# Revit family: NBS_Allermuir_OffcChrs-en-us-Kin_HighBackStool
name_source: partatom
category: Furniture
revit_build: Autodesk Revit 2018 (Build: 20190510_1515(x64)
units: mm (PartAtom-declared; Revit-internal decimal feet)

## family parameters
Always vertical = Yes
Cut with Voids When Loaded = No
Room Calculation Point = No
Shared = No
Work Plane-Based = No

## types (1)
- Kin_HighBackStool_KIN602
    AssetType = Movable
    BIMObjectName = NBS_Allermuir_OfficeChairs_Kin_HighBackStool_KIN602-US
    Category = Pr_40_50_12_57:Office chairs
    CodePerformance = ANSI/BIFMA X5.1-2017
    Color = Off-Black, White, Crayon Gray, Pistachio, Haze Blue, Aubergine, Seattle Green, Red
    Description = High back stool on 4 leg frame
    DurationUnit = year
    ExpectedLife = 10
    Features = Plastic shell — color: Off-Black, Tubular steel frame finished in Off-Black powder coat, Footrest protector, Plastic glides, Counter height option available, Plastic glides with felt
    Finish = Off-Black, White, Crayon Gray, Pistachio, Haze Blue, Aubergine, Seattle Green, Red
    FrameFinish = Off black, white, crayon gray, pistachio, seattle green, aubergine, red, haze blue
    FrameMaterial = NBS_Allermuir_Steel_BlackPowderCoat
    HighestSeatingHeight = 0 "
    IfcExportAs = IfcFurnitureType
    IfcExportType = STOOL
    IsBuiltIn = No
    LowestSeatingHeight = 0 "
    ManufacturerName = Allermuir
    ManufacturerURL = www.allermuir.com
    Material = Polypropylene, Aluminum Casting
    ModelNumber = KIN602
    ModelReference = Kin_HighBackStool
    NBSCertification = www.nationalbimlibrary.com/cert/i4pnqn2i
    NBSDescription = Office chairs
    NBSReference = 45-35-20/330
    Name = OfficeChairs_KIN602_Kin_Allermuir
    NominalDepth = 21 "
    NominalHeight = 44 "
    NominalLength = 18 "
    NominalWidth = 18 "
    OmniClassCode = 22-12 52 23
    OmniClassTitle = Office Seating
    OmniClassVersion = Table 22 2012-05-16
    ProductInformation = https://www.allermuir.com
    SeatDepth = 21"
    SeatMaterial = NBS_Allermuir_Plastic_Black
    SeatWidth = 18"
    SeatingHeight = 29 "
    Size = 21 x 44 x 18"
    Status = UNSET
    Style = Stool
    SustainabilityPerformance = 99% recyclable
    Uniclass2015Code = Pr_40_50_12_57
    Uniclass2015Title = Office chairs
    Uniclass2015Version = Products v1.15
    Version = 1
    WarrantyDescription = Allermuir warrant that its manufactured products are free from manufacturing defects - in materials or workmanship - for a period of ten (10) years. , Allermuir will repair, or replace (at Allermuir's sole discretion) with comparable free of charge materials / components, any product / component which fails under normal use in a single shift environment, as a result of a defect in the materials and/ or workmanship
    WarrantyDurationParts = 10
    WarrantyDurationUnit = year

## geometry (parser evidence)
native form markers: Sweep x3
no freeform markers — native parametric forms only
